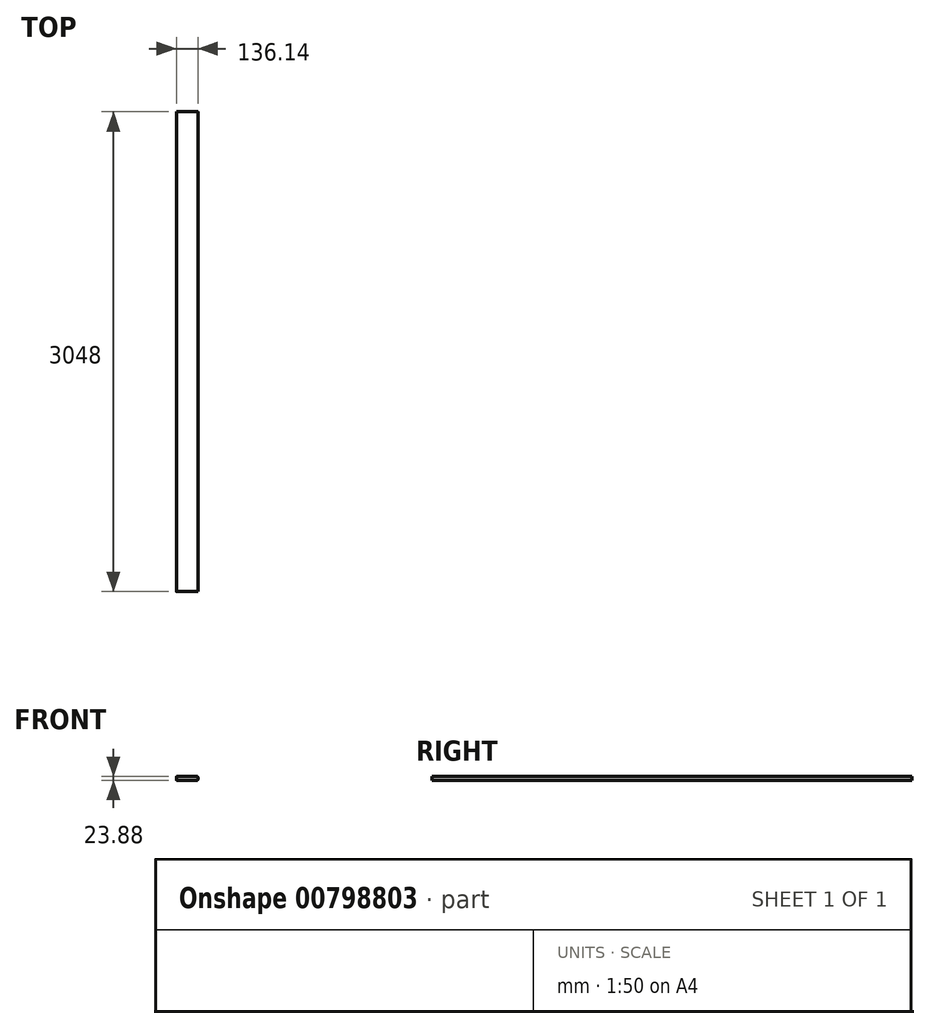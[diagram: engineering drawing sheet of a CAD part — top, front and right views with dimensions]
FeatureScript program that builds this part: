
annotation { "Feature Type Name" : "Feature", "Feature Type Description" : "" }
export const myFeature = defineFeature(function(context is Context, id is Id, definition is map)
    precondition{}
    {
        {
            var Q0;
            Q0=qCreatedBy(makeId("Front.planeOp"),FACE);
            var sketch = newSketch(context, id + "F0", { "sketchPlane" : qUnion([Q0])});
            skLineSegment(sketch, "E0.bottom", {"start": v(-63.25, 11.94) * mm, "end": v(63.25, 11.94) * mm});
            skLineSegment(sketch, "E0.top", {"start": v(-63.25, -11.94) * mm, "end": v(63.25, -11.94) * mm});
            skLineSegment(sketch, "E0.left", {"start": v(-68.07, 7.11) * mm, "end": v(-68.07, -7.11) * mm});
            skLineSegment(sketch, "E0.right", {"start": v(68.07, 7.11) * mm, "end": v(68.07, -7.11) * mm});
            skPoint(sketch, "E0.middle", {"position": v(0, 0) * mm});
            skPoint(sketch, "E1.visualSharp", {"position": v(-68.07, 11.94) * mm});
            skArc(sketch, "E1.filletArc", {"start": v(-63.25, 11.94) * mm, "mid": v(-66.66, 10.52) * mm, "end": v(-68.07, 7.11) * mm});
            skPoint(sketch, "E2.visualSharp", {"position": v(68.07, 11.94) * mm});
            skArc(sketch, "E2.filletArc", {"start": v(68.07, 7.11) * mm, "mid": v(66.66, 10.52) * mm, "end": v(63.25, 11.94) * mm});
            skPoint(sketch, "E3.visualSharp", {"position": v(68.07, -11.94) * mm});
            skArc(sketch, "E3.filletArc", {"start": v(63.25, -11.94) * mm, "mid": v(66.66, -10.52) * mm, "end": v(68.07, -7.11) * mm});
            skPoint(sketch, "E4.visualSharp", {"position": v(-68.07, -11.94) * mm});
            skArc(sketch, "E4.filletArc", {"start": v(-68.07, -7.11) * mm, "mid": v(-66.66, -10.52) * mm, "end": v(-63.25, -11.94) * mm});
            skSolve(sketch);
        }
        {
            var Q0;
            Q0=makeQuery(id+"F0.imprint","IMPRINT",FACE,{"disambiguationData":[TD([[makeQuery(id+"F0.imprint","IMPRINT",EDGE,{"derivedFrom":sQuery(id+"F0.wireOp",EDGE,"E0.bottom")}),-1.0]])]});
            extrude(context, id + "F1", {"entities" : qUnion([Q0]), "endBound" : BoundingType.SYMMETRIC, "depth" : 3048 * mm, "offsetDistance" : 25.4 * mm});
        }
    });
